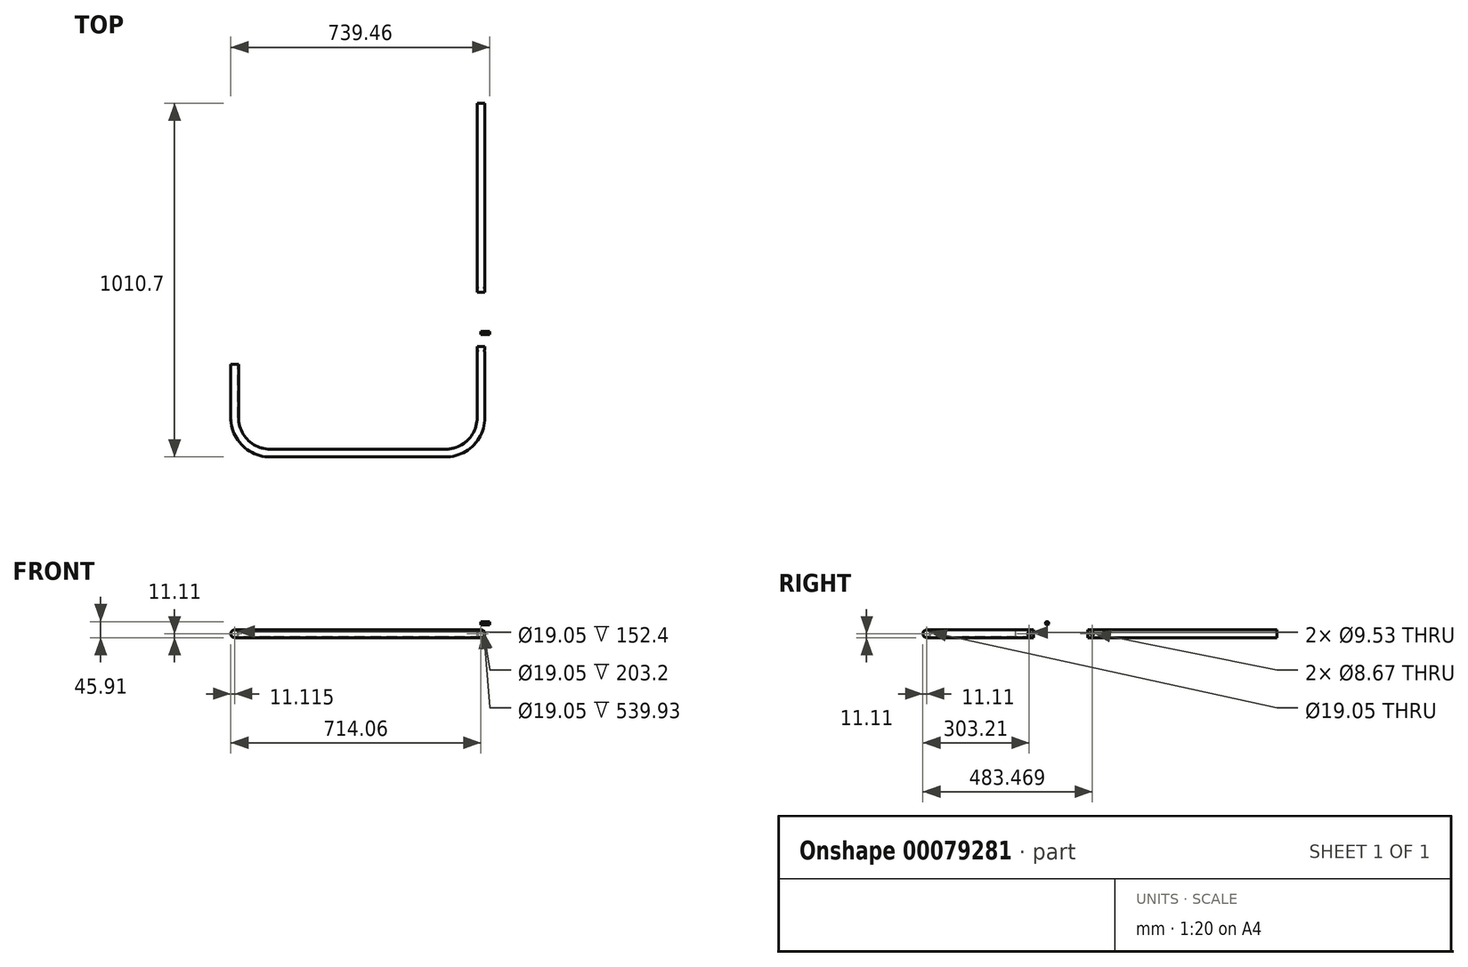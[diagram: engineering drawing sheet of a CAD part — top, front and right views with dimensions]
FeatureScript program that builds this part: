
annotation { "Feature Type Name" : "Feature", "Feature Type Description" : "" }
export const myFeature = defineFeature(function(context is Context, id is Id, definition is map)
    precondition{}
    {
        {
            var Q0;
            Q0=qCreatedBy(makeId("Top.planeOp"),FACE);
            var sketch = newSketch(context, id + "F0", { "sketchPlane" : qUnion([Q0])});
            skLineSegment(sketch, "E0", {"start": v(0, 0) * mm, "end": v(0, -203.2) * mm});
            skLineSegment(sketch, "E1", {"start": v(-101.6, -304.8) * mm, "end": v(-601.35, -304.8) * mm});
            skLineSegment(sketch, "E2", {"start": v(-702.95, -203.2) * mm, "end": v(-702.95, -50.8) * mm});
            skPoint(sketch, "E3.visualSharp", {"position": v(-702.95, -304.8) * mm});
            skArc(sketch, "E3.filletArc", {"start": v(-702.95, -203.2) * mm, "mid": v(-673.19, -275.04) * mm, "end": v(-601.35, -304.8) * mm});
            skPoint(sketch, "E4.visualSharp", {"position": v(0, -304.8) * mm});
            skArc(sketch, "E4.filletArc", {"start": v(-101.6, -304.8) * mm, "mid": v(-29.76, -275.04) * mm, "end": v(0, -203.2) * mm});
            skLineSegment(sketch, "E5", {"start": v(0, -128.63) * mm, "end": v(-702.95, -136.46) * mm});
            skPoint(sketch, "E6", {"position": v(-702.95, -127) * mm});
            skSolve(sketch);
        }
        {
            var Q0;
            Q0=qCreatedBy(makeId("Front.planeOp"),FACE);
            var sketch = newSketch(context, id + "F1", { "sketchPlane" : qUnion([Q0])});
            skCircle(sketch, "E7", {"center": v(0, 0) * mm, "radius": 11.11 * mm});
            skCircle(sketch, "E8", {"center": v(0, 0) * mm, "radius": 9.53 * mm});
            skSolve(sketch);
        }
        {
            var Q0;
            Q0 = qSketchRegion(id + "F1", true);
            var Q1;
            Q1=sQuery(id+"F0.wireOp",EDGE,"E0");
            var Q2;
            Q2=sQuery(id+"F0.wireOp",EDGE,"E4.filletArc");
            var Q3;
            Q3=sQuery(id+"F0.wireOp",EDGE,"E1");
            var Q4;
            Q4=sQuery(id+"F0.wireOp",EDGE,"E3.filletArc");
            var Q5;
            Q5=sQuery(id+"F0.wireOp",EDGE,"E2");
            sweep(context, id + "F2", {"profiles" : qUnion([Q0]), "path" : qUnion([Q1, Q2, Q3, Q4, Q5])});
        }
        {
            var Q0;
            Q0=qCreatedBy(makeId("Top.planeOp"),FACE);
            var sketch = newSketch(context, id + "F3", { "sketchPlane" : qUnion([Q0])});
            skLineSegment(sketch, "E9", {"start": v(0, 154.86) * mm, "end": v(0, 694.79) * mm});
            skLineSegment(sketch, "E10", {"start": v(-701.66, 154.86) * mm, "end": v(-701.66, 733.18) * mm});
            skSolve(sketch);
        }
        {
            var Q0;
            Q0=sQuery(id+"F3.wireOp",VERTEX,"E9.start");
            var Q1;
            Q1=qCreatedBy(makeId("Front.planeOp"),FACE);
            cPlane(context, id + "F4", {"entities" : qUnion([Q0, Q1]), "cplaneType" : CPlaneType.PLANE_POINT, "offset" : 152.4 * mm, "width" : 152.4 * mm, "height" : 152.4 * mm});
        }
        {
            var Q0;
            Q0=qCreatedBy(id+"F4.planeOp",FACE);
            var sketch = newSketch(context, id + "F5", { "sketchPlane" : qUnion([Q0])});
            skCircle(sketch, "E11", {"center": v(0, 0) * mm, "radius": 11.11 * mm});
            skCircle(sketch, "E12", {"center": v(0, 0) * mm, "radius": 9.53 * mm});
            skSolve(sketch);
        }
        {
            var Q0;
            Q0 = qSketchRegion(id + "F5", true);
            var Q1;
            Q1=sQuery(id+"F3.wireOp",EDGE,"E9");
            sweep(context, id + "F6", {"profiles" : qUnion([Q0]), "path" : qUnion([Q1])});
        }
        {
            var Q0;
            Q0=qCreatedBy(makeId("Right.planeOp"),FACE);
            var sketch = newSketch(context, id + "F7", { "sketchPlane" : qUnion([Q0])});
            skCircle(sketch, "E13", {"center": v(-12.7, 0) * mm, "radius": 4.76 * mm});
            skCircle(sketch, "E14", {"center": v(167.56, 0) * mm, "radius": 4.33 * mm});
            skSolve(sketch);
        }
        {
            var Q0;
            Q0 = qSketchRegion(id + "F7", true);
            extrude(context, id + "F8", {"entities" : qUnion([Q0]), "operationType" : NewBodyOperationType.REMOVE, "endBound" : BoundingType.SYMMETRIC, "oppositeDirection" : true, "depth" : 25.4 * mm});
        }
        {
            var Q0;
            Q0=qCreatedBy(makeId("Right.planeOp"),FACE);
            var sketch = newSketch(context, id + "F9", { "sketchPlane" : qUnion([Q0])});
            skCircle(sketch, "E15", {"center": v(38.58, 30.04) * mm, "radius": 4.76 * mm});
            skSolve(sketch);
        }
        {
            var Q0;
            Q0=makeQuery(id+"F9.imprint","IMPRINT",FACE,{"disambiguationData":[TD([[makeQuery(id+"F9.imprint","IMPRINT",EDGE,{"derivedFrom":sQuery(id+"F9.wireOp",EDGE,"E15")}),1.0]])]});
            extrude(context, id + "F10", {"entities" : qUnion([Q0]), "depth" : 25.4 * mm});
        }
    });
